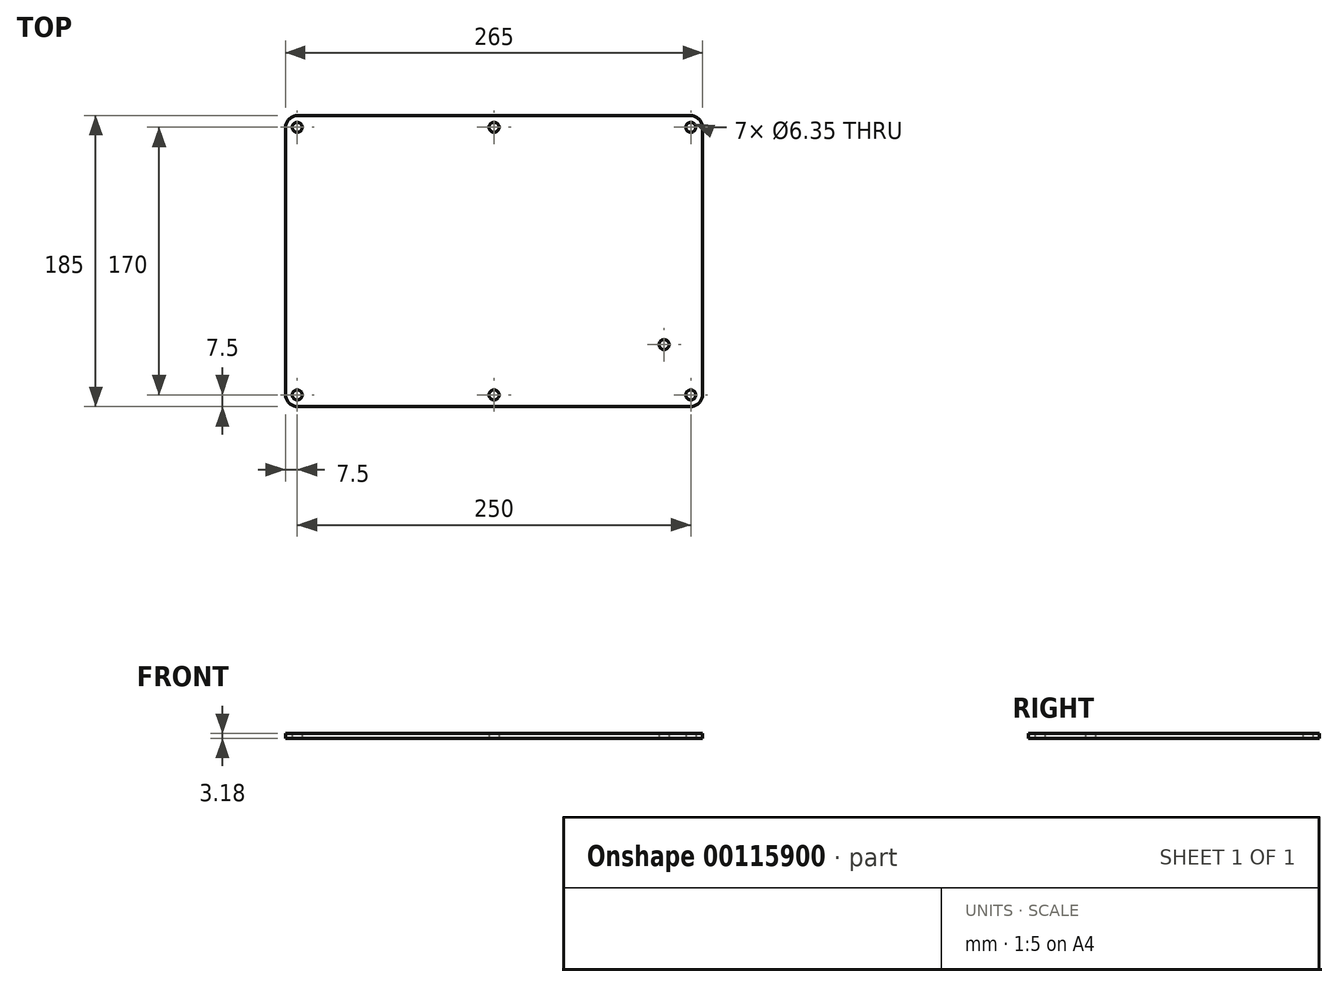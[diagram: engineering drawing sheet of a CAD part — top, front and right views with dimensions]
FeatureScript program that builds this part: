
annotation { "Feature Type Name" : "Feature", "Feature Type Description" : "" }
export const myFeature = defineFeature(function(context is Context, id is Id, definition is map)
    precondition{}
    {
        {
            var Q0;
            Q0=qCreatedBy(makeId("Top.planeOp"),FACE);
            var sketch = newSketch(context, id + "F0", { "sketchPlane" : qUnion([Q0])});
            skLineSegment(sketch, "E0.rect.bottom", {"start": v(-132.5, 92.5) * mm, "end": v(132.5, 92.5) * mm});
            skLineSegment(sketch, "E0.rect.top", {"start": v(-132.5, -92.5) * mm, "end": v(132.5, -92.5) * mm});
            skLineSegment(sketch, "E0.rect.left", {"start": v(-132.5, 92.5) * mm, "end": v(-132.5, -92.5) * mm});
            skLineSegment(sketch, "E0.rect.right", {"start": v(132.5, 92.5) * mm, "end": v(132.5, -92.5) * mm});
            skPoint(sketch, "E0.rect.middle", {"position": v(0, 0) * mm});
            skCircle(sketch, "E1", {"center": v(0, 85) * mm, "radius": 3.18 * mm});
            skLineSegment(sketch, "E2", {"start": v(0, 0) * mm, "end": v(-132.5, 0) * mm, "construction": true});
            skLineSegment(sketch, "E3", {"start": v(0, 0) * mm, "end": v(0, 92.5) * mm, "construction": true});
            skCircle(sketch, "E4", {"center": v(-125, 85) * mm, "radius": 3.18 * mm});
            skCircle(sketch, "E5.0.MirrorC", {"center": v(125, 85) * mm, "radius": 3.18 * mm});
            skCircle(sketch, "E6.0.MirrorC", {"center": v(0, -85) * mm, "radius": 3.18 * mm});
            skCircle(sketch, "E7.0.MirrorC", {"center": v(-125, -85) * mm, "radius": 3.18 * mm});
            skCircle(sketch, "E8.0.MirrorC", {"center": v(125, -85) * mm, "radius": 3.18 * mm});
            skCircle(sketch, "E9", {"center": v(108.02, -53.02) * mm, "radius": 3.18 * mm});
            skSolve(sketch);
        }
        {
            var Q0;
            Q0=qSketchRegion(id+"F0",true);
            extrude(context, id + "F1", {"entities" : qUnion([Q0]), "depth" : 3.17 * mm});
        }
        {
            var Q0;
            Q0=makeQuery(id+"F1.opExtrude","SWEPT_EDGE",EDGE,{"disambiguationData":[OSD([sQuery(id+"F0.wireOp",EDGE,"E0.rect.bottom"),sQuery(id+"F0.wireOp",EDGE,"E0.rect.left")])]});
            var Q1;
            Q1=makeQuery(id+"F1.opExtrude","SWEPT_EDGE",EDGE,{"disambiguationData":[OSD([sQuery(id+"F0.wireOp",EDGE,"E0.rect.bottom"),sQuery(id+"F0.wireOp",EDGE,"E0.rect.right")])]});
            var Q2;
            Q2=makeQuery(id+"F1.opExtrude","SWEPT_EDGE",EDGE,{"disambiguationData":[OSD([sQuery(id+"F0.wireOp",EDGE,"E0.rect.top"),sQuery(id+"F0.wireOp",EDGE,"E0.rect.right")])]});
            var Q3;
            Q3=makeQuery(id+"F1.opExtrude","SWEPT_EDGE",EDGE,{"disambiguationData":[OSD([sQuery(id+"F0.wireOp",EDGE,"E0.rect.top"),sQuery(id+"F0.wireOp",EDGE,"E0.rect.left")])]});
            fillet(context, id + "F2", {"entities" : qUnion([Q0, Q1, Q2, Q3]), "radius" : 8 * mm, "tangentPropagation" : true, "allowEdgeOverflow" : false});
        }
    });
